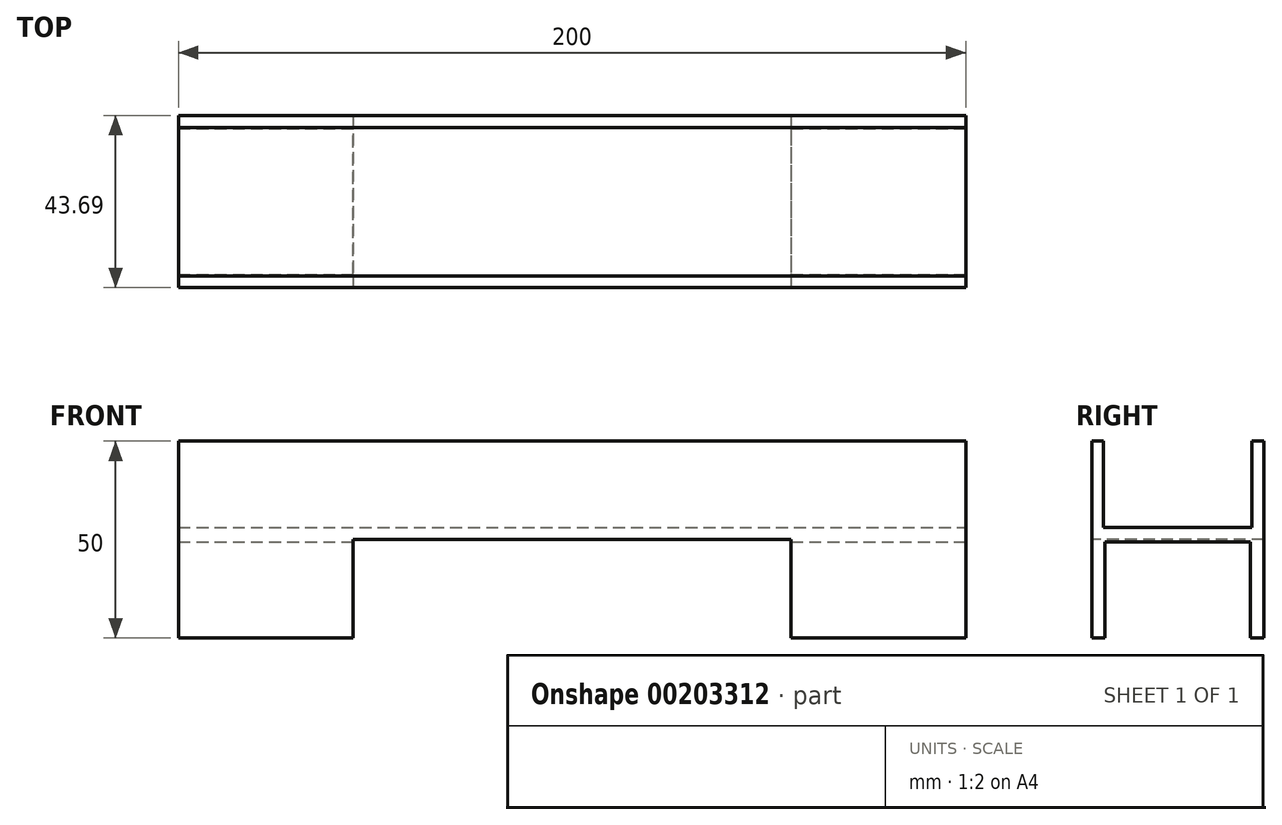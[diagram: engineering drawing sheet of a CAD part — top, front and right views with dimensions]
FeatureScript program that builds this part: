
annotation { "Feature Type Name" : "Feature", "Feature Type Description" : "" }
export const myFeature = defineFeature(function(context is Context, id is Id, definition is map)
    precondition{}
    {
        {
            var Q0;
            Q0=qCreatedBy(makeId("Front.planeOp"),FACE);
            var sketch = newSketch(context, id + "F0", { "sketchPlane" : qUnion([Q0])});
            skLineSegment(sketch, "E0.bottom", {"start": v(100, 12.5) * mm, "end": v(-100, 12.5) * mm});
            skLineSegment(sketch, "E0.top", {"start": v(100, -12.5) * mm, "end": v(-100, -12.5) * mm});
            skLineSegment(sketch, "E0.left", {"start": v(100, 12.5) * mm, "end": v(100, -12.5) * mm});
            skLineSegment(sketch, "E0.right", {"start": v(-100, 12.5) * mm, "end": v(-100, -12.5) * mm});
            skPoint(sketch, "E0.middle", {"position": v(0, 0) * mm});
            skSolve(sketch);
        }
        {
            var Q0;
            Q0=makeQuery(id+"F0.imprint","IMPRINT",FACE,{"disambiguationData":[TD([[makeQuery(id+"F0.imprint","IMPRINT",EDGE,{"derivedFrom":sQuery(id+"F0.wireOp",EDGE,"E0.bottom")}),1.0]])]});
            extrude(context, id + "F1", {"entities" : qUnion([Q0]), "depth" : 43.69 * mm});
        }
        {
            var Q0;
            Q0=makeQuery(id+"F1.opExtrude","SWEPT_FACE",FACE,{"disambiguationData":[OSD([sQuery(id+"F0.wireOp",EDGE,"E0.left")])]});
            var sketch = newSketch(context, id + "F2", { "sketchPlane" : qUnion([Q0])});
            skLineSegment(sketch, "E1.bottom", {"start": v(-40.69, 12.5) * mm, "end": v(-3, 12.5) * mm});
            skLineSegment(sketch, "E1.top", {"start": v(-40.69, -9.5) * mm, "end": v(-3, -9.5) * mm});
            skLineSegment(sketch, "E1.left", {"start": v(-40.69, 12.5) * mm, "end": v(-40.69, -9.5) * mm});
            skLineSegment(sketch, "E1.right", {"start": v(-3, 12.5) * mm, "end": v(-3, -9.5) * mm});
            skLineSegment(sketch, "E2", {"start": v(-43.69, 6.48) * mm, "end": v(-40.69, 6.48) * mm, "construction": true});
            skLineSegment(sketch, "E3", {"start": v(-12.1, -9.5) * mm, "end": v(-12.1, -12.5) * mm, "construction": true});
            skLineSegment(sketch, "E4", {"start": v(-3, 6.88) * mm, "end": v(0, 6.88) * mm, "construction": true});
            skSolve(sketch);
        }
        {
            var Q0;
            Q0=makeQuery(id+"F2.imprint","IMPRINT",FACE,{"disambiguationData":[TD([[makeQuery(id+"F2.imprint","IMPRINT",EDGE,{"derivedFrom":sQuery(id+"F2.wireOp",EDGE,"E1.bottom")}),-1.0]])]});
            extrude(context, id + "F3", {"entities" : qUnion([Q0]), "operationType" : NewBodyOperationType.REMOVE, "endBound" : BoundingType.THROUGH_ALL, "oppositeDirection" : true, "depth" : 25.4 * mm});
        }
        {
            var Q0;
            Q0=makeQuery(id+"F1.opExtrude","SWEPT_FACE",FACE,{"disambiguationData":[OSD([sQuery(id+"F0.wireOp",EDGE,"E0.top")])]});
            var sketch = newSketch(context, id + "F4", { "sketchPlane" : qUnion([Q0])});
            skLineSegment(sketch, "E5.bottom", {"start": v(100, 0) * mm, "end": v(55.65, 0) * mm});
            skLineSegment(sketch, "E5.top", {"start": v(100, 43.69) * mm, "end": v(55.65, 43.69) * mm});
            skLineSegment(sketch, "E5.left", {"start": v(100, 0) * mm, "end": v(100, 43.69) * mm});
            skLineSegment(sketch, "E5.right", {"start": v(55.65, 0) * mm, "end": v(55.65, 43.69) * mm});
            skSolve(sketch);
        }
        {
            var Q0;
            Q0 = qSketchRegion(id + "F4", true);
            extrude(context, id + "F5", {"entities" : qUnion([Q0]), "depth" : 25 * mm});
        }
        {
            var Q0;
            Q0=makeQuery(id+"F5.opExtrude","SWEPT_BODY",BODY,{"disambiguationData":[OSD([sQuery(id+"F4.wireOp",EDGE,"E5.bottom"),sQuery(id+"F4.wireOp",EDGE,"E5.top"),sQuery(id+"F4.wireOp",EDGE,"E5.left"),sQuery(id+"F4.wireOp",EDGE,"E5.right")])]});
            var Q1;
            Q1=qCreatedBy(makeId("Right.planeOp"),FACE);
            mirror(context, id + "F6", {"operationType" : NewBodyOperationType.ADD, "entities" : qUnion([Q0]), "mirrorPlane" : qUnion([Q1])});
        }
        {
            var Q0;
            Q0=makeQuery(id+"F6.boolean.opBoolean","MERGE",FACE,{"derivedFrom":[makeQuery(id+"F1.opExtrude","SWEPT_FACE",FACE,{"disambiguationData":[OSD([sQuery(id+"F0.wireOp",EDGE,"E0.left")])]}),makeQuery(id+"F5.opExtrude","SWEPT_FACE",FACE,{"disambiguationData":[OSD([sQuery(id+"F4.wireOp",EDGE,"E5.left")])]})]});
            var sketch = newSketch(context, id + "F7", { "sketchPlane" : qUnion([Q0])});
            skLineSegment(sketch, "E6.bottom", {"start": v(-40.32, -37.5) * mm, "end": v(-3.33, -37.5) * mm});
            skLineSegment(sketch, "E6.top", {"start": v(-40.32, -13.18) * mm, "end": v(-3.33, -13.18) * mm});
            skLineSegment(sketch, "E6.left", {"start": v(-40.32, -37.5) * mm, "end": v(-40.32, -13.18) * mm});
            skLineSegment(sketch, "E6.right", {"start": v(-3.33, -37.5) * mm, "end": v(-3.33, -13.18) * mm});
            skSolve(sketch);
        }
        {
            var Q0;
            Q0=makeQuery(id+"F7.imprint","IMPRINT",FACE,{"disambiguationData":[TD([[makeQuery(id+"F7.imprint","IMPRINT",EDGE,{"derivedFrom":sQuery(id+"F7.wireOp",EDGE,"E6.bottom")}),1.0]])]});
            extrude(context, id + "F8", {"entities" : qUnion([Q0]), "operationType" : NewBodyOperationType.REMOVE, "endBound" : BoundingType.THROUGH_ALL, "oppositeDirection" : true, "depth" : 25.4 * mm});
        }
    });
